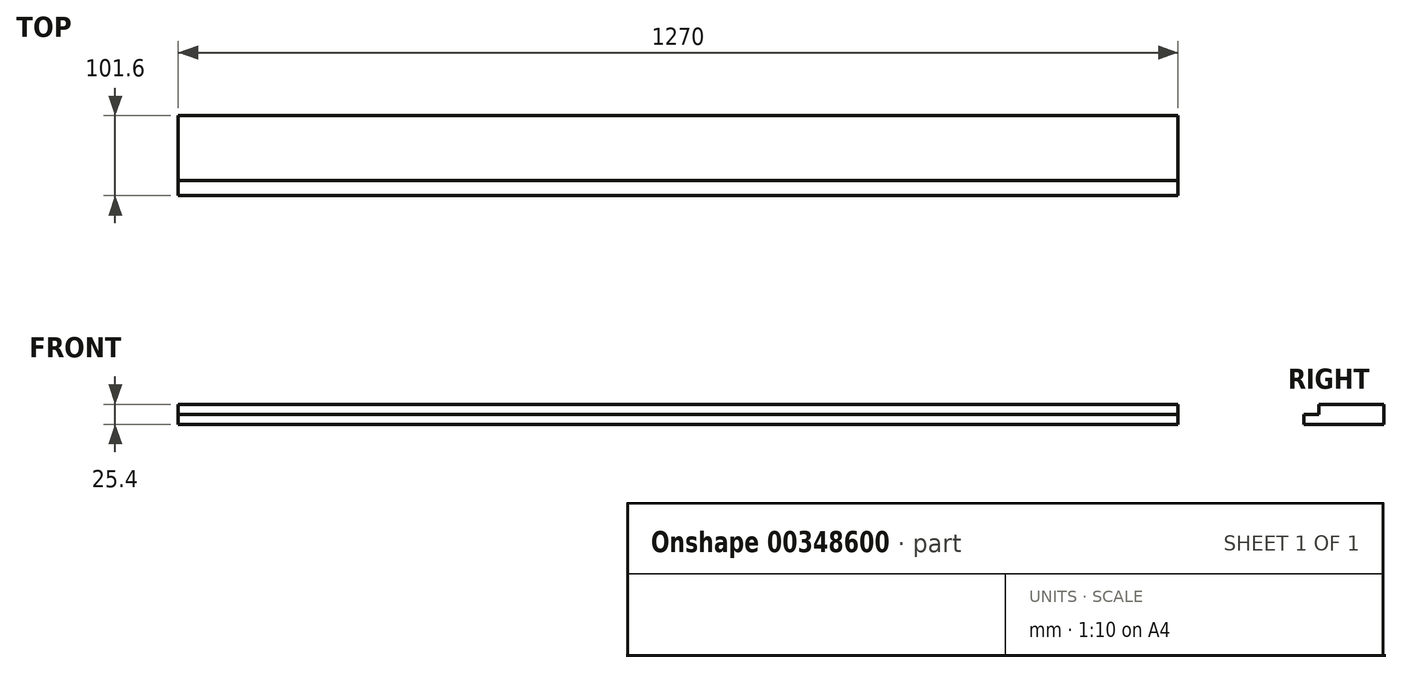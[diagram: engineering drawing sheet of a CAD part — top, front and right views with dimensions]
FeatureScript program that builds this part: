
annotation { "Feature Type Name" : "Feature", "Feature Type Description" : "" }
export const myFeature = defineFeature(function(context is Context, id is Id, definition is map)
    precondition{}
    {
        {
            var Q0;
            Q0=qCreatedBy(makeId("Top.planeOp"),FACE);
            var sketch = newSketch(context, id + "F0", { "sketchPlane" : qUnion([Q0])});
            skLineSegment(sketch, "E0.bottom", {"start": v(-256.04, 59.7) * mm, "end": v(1013.96, 59.7) * mm});
            skLineSegment(sketch, "E0.top", {"start": v(-256.04, -41.9) * mm, "end": v(1013.96, -41.9) * mm});
            skLineSegment(sketch, "E0.left", {"start": v(-256.04, 59.7) * mm, "end": v(-256.04, -41.9) * mm});
            skLineSegment(sketch, "E0.right", {"start": v(1013.96, 59.7) * mm, "end": v(1013.96, -41.9) * mm});
            skLineSegment(sketch, "E1", {"start": v(-256.04, -22.84) * mm, "end": v(1013.96, -22.84) * mm});
            skSolve(sketch);
        }
        {
            var Q0;
            {var subQ0=sQuery(id+"F0.wireOp",EDGE,"E0.bottom");Q0=makeQuery(id+"F0.imprint","IMPRINT",FACE,{"disambiguationData":[TD([[makeQuery(id+"F0.imprint","IMPRINT",EDGE,{"derivedFrom":subQ0}),-1.0]])]});}
            extrude(context, id + "F1", {"entities" : qUnion([Q0]), "depth" : 12.7 * mm});
        }
        {
            var Q0;
            Q0=qSketchRegion(id+"F0",true);
            var Q1;
            Q1=makeQuery(id+"F1.opExtrude","CAP_FACE",FACE,{"disambiguationData":[OSD([sQuery(id+"F0.wireOp",EDGE,"E0.bottom"),sQuery(id+"F0.wireOp",EDGE,"E0.left"),sQuery(id+"F0.wireOp",EDGE,"E0.right"),sQuery(id+"F0.wireOp",EDGE,"E1")])],"isStart":false});
            extrude(context, id + "F2", {"entities" : qUnion([Q0, Q1]), "operationType" : NewBodyOperationType.ADD, "depth" : 12.7 * mm});
        }
    });
